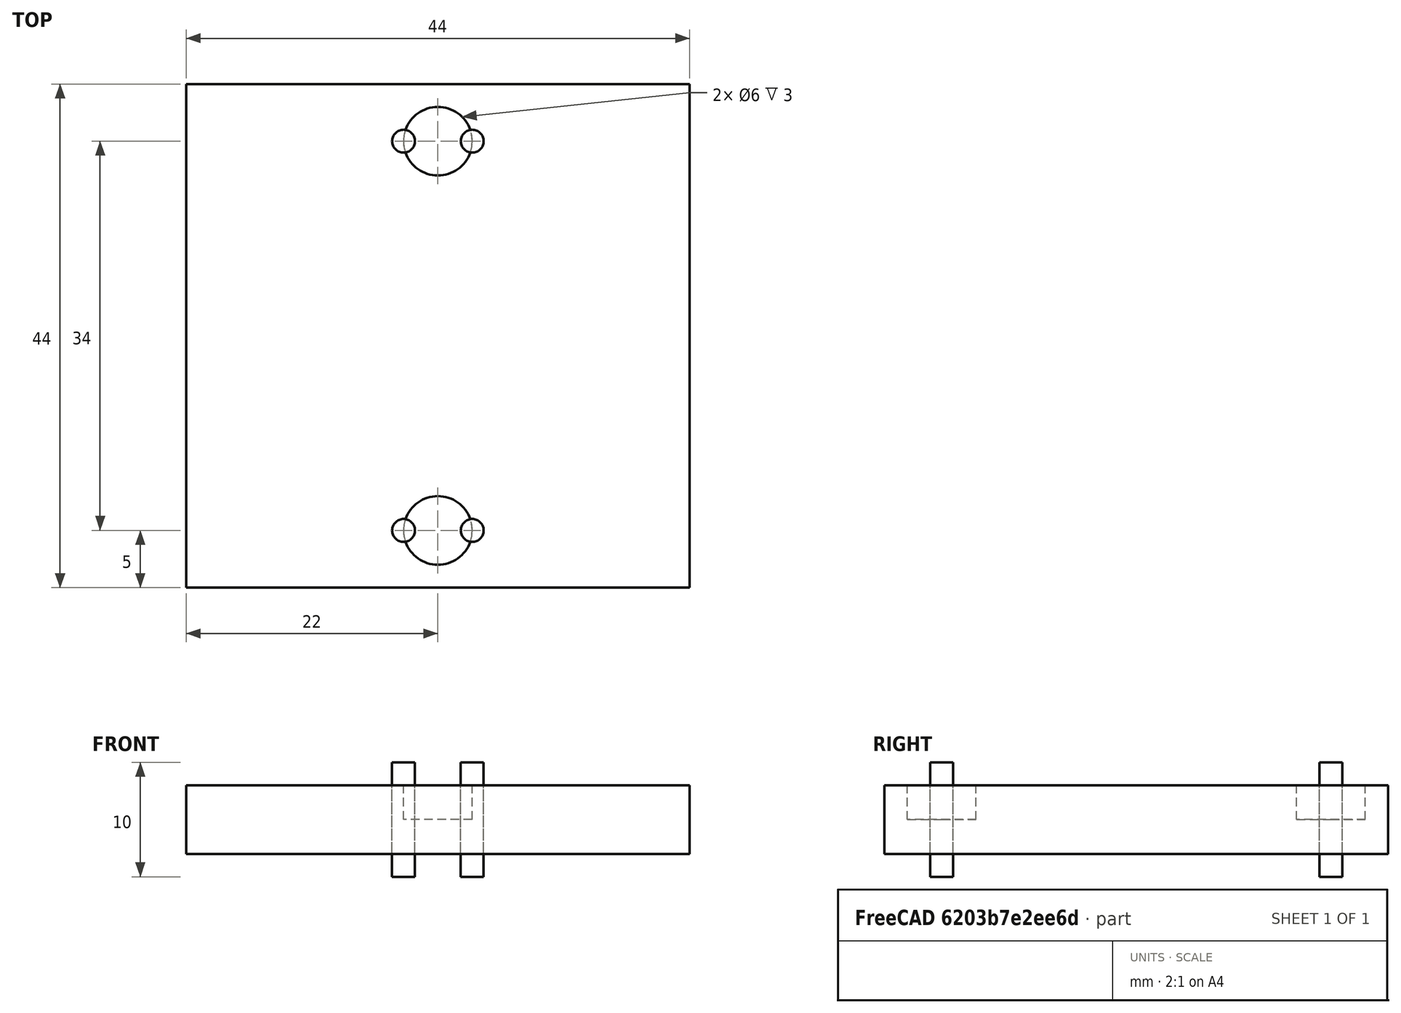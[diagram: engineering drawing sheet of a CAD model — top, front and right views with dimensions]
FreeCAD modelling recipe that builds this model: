
FCSTD DOCUMENT  (FreeCAD 0.16R)
Label: bottom-part2
License: All rights reserved
LicenseURL: http://en.wikipedia.org/wiki/All_rights_reserved
objects: Part::Cylinder×6, Part::Cut×2, Part::Box×1
note: 9 computed .brp shape members not serialized (recipe doc carries the construction recipe); baked Part::Feature solids carry a one-line shape summary decoded from their .brp

FEATURE [Part::Box] Box  label="Cube"
  Height = 6
  Length = 44
  Width = 44
FEATURE [Part::Cylinder] Cylinder
  Angle = 360
  Height = 10
  Placement = pos=(22,5,3) rot=(0,0,1;0rad)
  Radius = 3
FEATURE [Part::Cylinder] Cylinder001
  Angle = 360
  Height = 10
  Placement = pos=(22,39,3) rot=(0,0,1;0rad)
  Radius = 3
FEATURE [Part::Cut] Cut
  Base = -> Box
  Tool = -> Cylinder001
FEATURE [Part::Cut] Cut001
  Base = -> Cut
  Tool = -> Cylinder
FEATURE [Part::Cylinder] Cylinder002
  Angle = 360
  Height = 10
  Placement = pos=(19,5,-2) rot=(0,0,1;0rad)
  Radius = 1
FEATURE [Part::Cylinder] Cylinder003
  Angle = 360
  Height = 10
  Placement = pos=(25,5,-2) rot=(0,0,1;0rad)
  Radius = 1
FEATURE [Part::Cylinder] Cylinder004
  Angle = 360
  Height = 10
  Placement = pos=(19,39,-2) rot=(0,0,1;0rad)
  Radius = 1
FEATURE [Part::Cylinder] Cylinder005
  Angle = 360
  Height = 10
  Placement = pos=(25,39,-2) rot=(0,0,1;0rad)
  Radius = 1
